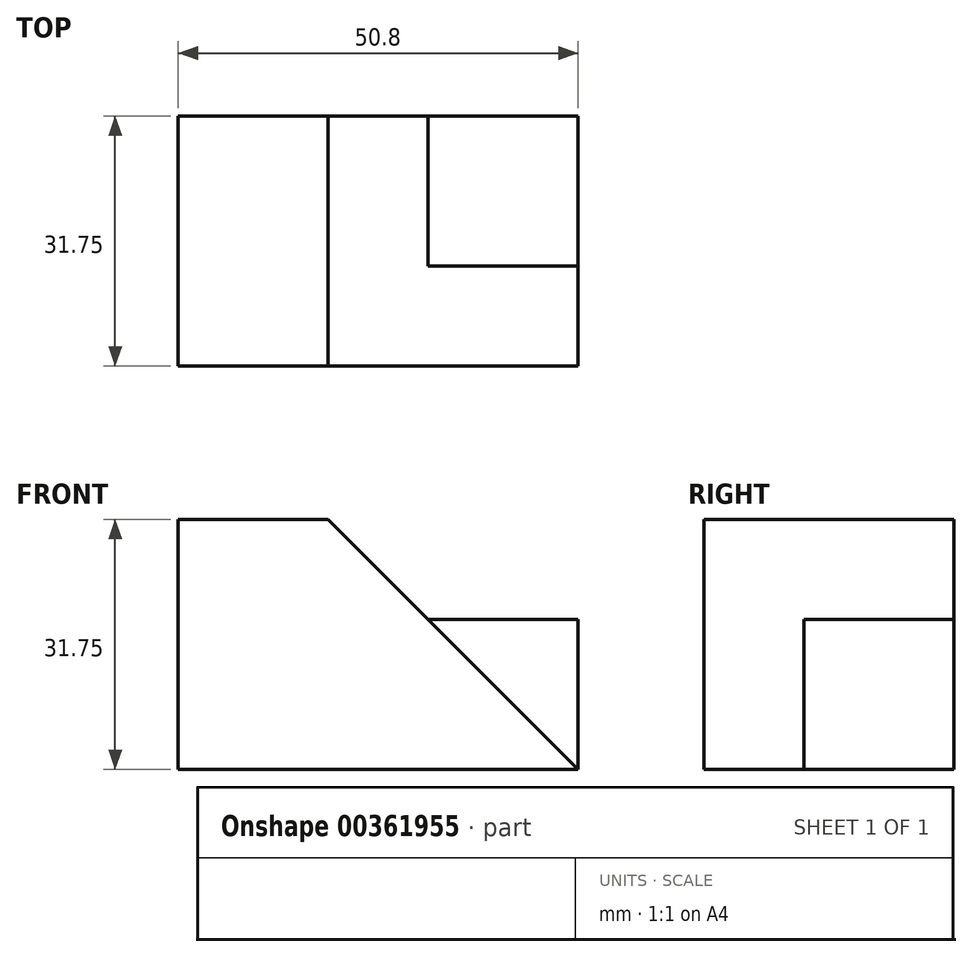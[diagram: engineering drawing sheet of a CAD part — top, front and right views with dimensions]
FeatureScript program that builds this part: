
annotation { "Feature Type Name" : "Feature", "Feature Type Description" : "" }
export const myFeature = defineFeature(function(context is Context, id is Id, definition is map)
    precondition{}
    {
        {
            var Q0;
            Q0=qCreatedBy(makeId("Front.planeOp"),FACE);
            var sketch = newSketch(context, id + "F0", { "sketchPlane" : qUnion([Q0])});
            skLineSegment(sketch, "E0", {"start": v(0, 0) * mm, "end": v(0, 31.75) * mm});
            skLineSegment(sketch, "E1", {"start": v(0, 31.75) * mm, "end": v(50.8, 31.75) * mm});
            skLineSegment(sketch, "E2", {"start": v(50.8, 31.75) * mm, "end": v(50.8, 0) * mm});
            skLineSegment(sketch, "E3", {"start": v(50.8, 0) * mm, "end": v(0, 0) * mm});
            skSolve(sketch);
        }
        {
            var Q0;
            Q0=makeQuery(id+"F0.imprint","IMPRINT",FACE,{"disambiguationData":[TD([[makeQuery(id+"F0.imprint","IMPRINT",EDGE,{"derivedFrom":sQuery(id+"F0.wireOp",EDGE,"E0")}),-1.0]])]});
            extrude(context, id + "F1", {"entities" : qUnion([Q0]), "oppositeDirection" : true, "depth" : 31.75 * mm});
        }
        {
            var Q0;
            Q0=makeQuery(id+"F1.opExtrude","CAP_FACE",FACE,{"disambiguationData":[OSD([sQuery(id+"F0.wireOp",EDGE,"E0"),sQuery(id+"F0.wireOp",EDGE,"E1"),sQuery(id+"F0.wireOp",EDGE,"E2"),sQuery(id+"F0.wireOp",EDGE,"E3")])],"isStart":true});
            var sketch = newSketch(context, id + "F2", { "sketchPlane" : qUnion([Q0])});
            skLineSegment(sketch, "E4", {"start": v(19.05, 31.75) * mm, "end": v(50.8, 0) * mm});
            skSolve(sketch);
        }
        {
            var Q0;
            {var subQ0=sQuery(id+"F2.wireOp",EDGE,"E4");Q0=makeQuery(id+"F2.imprint","IMPRINT",FACE,{"disambiguationData":[TD([[makeQuery(id+"F2.imprint","IMPRINT",EDGE,{"derivedFrom":subQ0}),1.0]])]});}
            extrude(context, id + "F3", {"entities" : qUnion([Q0]), "operationType" : NewBodyOperationType.REMOVE, "oppositeDirection" : true, "depth" : 12.7 * mm});
        }
        {
            var Q0;
            Q0=makeQuery(id+"F3.boolean.opBoolean","COPY",FACE,{"derivedFrom":makeQuery(id+"F3.opExtrude","CAP_FACE",FACE,{"disambiguationData":[OSD([sQuery(id+"F0.wireOp",EDGE,"E1"),sQuery(id+"F0.wireOp",EDGE,"E2"),sQuery(id+"F2.wireOp",EDGE,"E4")])],"isStart":false})});
            var sketch = newSketch(context, id + "F4", { "sketchPlane" : qUnion([Q0])});
            skLineSegment(sketch, "E5", {"start": v(50.8, 19.05) * mm, "end": v(31.75, 19.05) * mm});
            skSolve(sketch);
        }
        {
            var Q0;
            {var subQ0=sQuery(id+"F4.wireOp",EDGE,"E5");Q0=makeQuery(id+"F4.imprint","IMPRINT",FACE,{"disambiguationData":[TD([[makeQuery(id+"F4.imprint","IMPRINT",EDGE,{"derivedFrom":subQ0}),-1.0]])]});}
            extrude(context, id + "F5", {"entities" : qUnion([Q0]), "operationType" : NewBodyOperationType.REMOVE, "oppositeDirection" : true, "depth" : 25.4 * mm});
        }
    });
